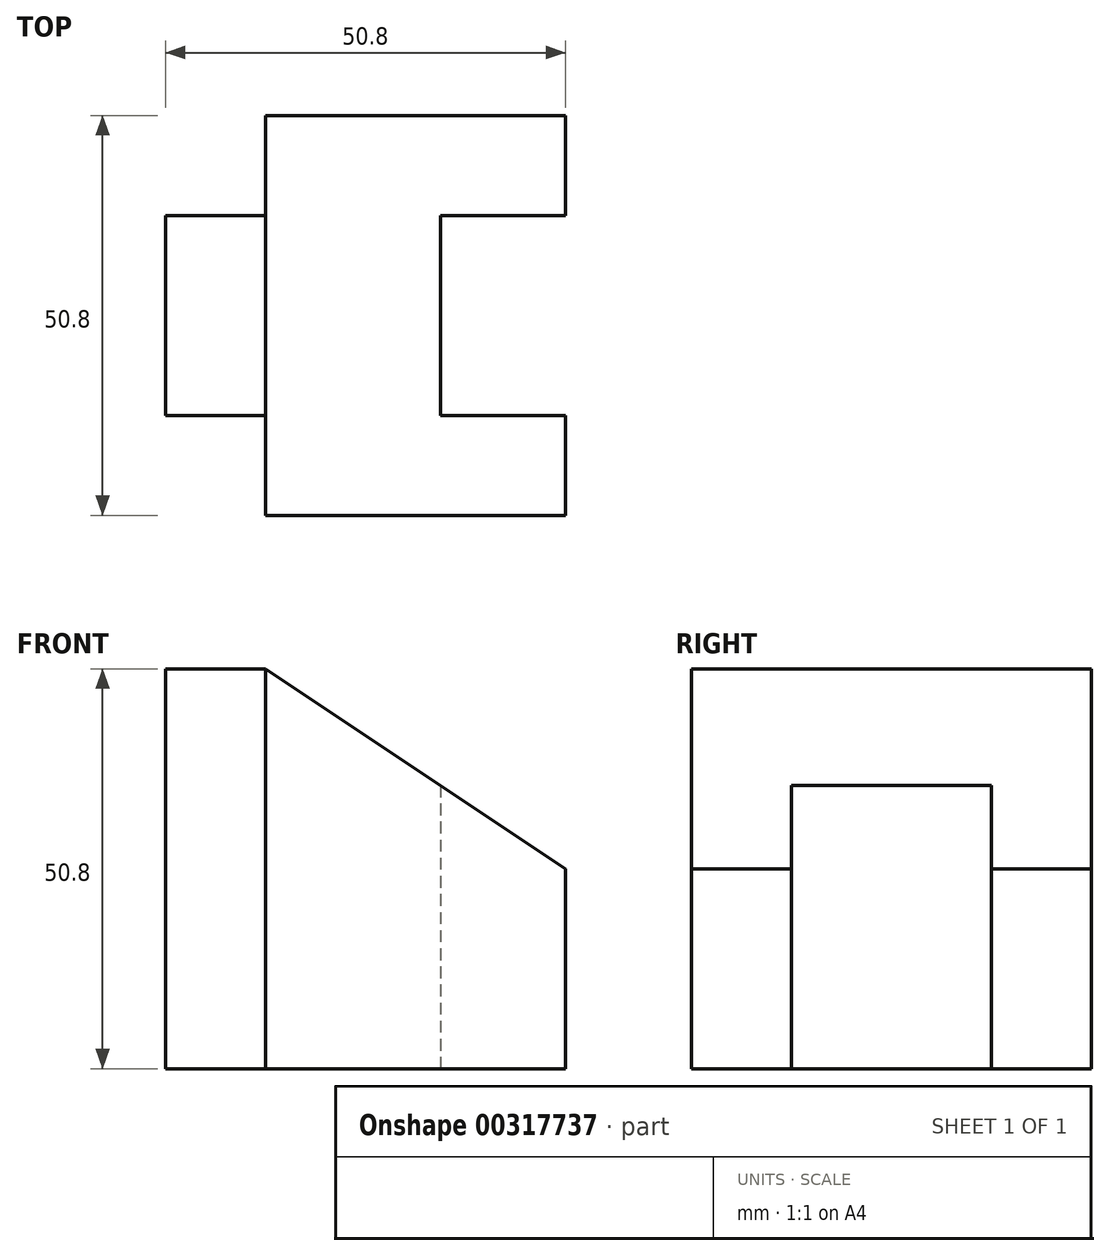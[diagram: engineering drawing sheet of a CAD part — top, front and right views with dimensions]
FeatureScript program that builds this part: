
annotation { "Feature Type Name" : "Feature", "Feature Type Description" : "" }
export const myFeature = defineFeature(function(context is Context, id is Id, definition is map)
    precondition{}
    {
        {
            var Q0;
            Q0=qCreatedBy(makeId("Front.planeOp"),FACE);
            var sketch = newSketch(context, id + "F0", { "sketchPlane" : qUnion([Q0])});
            skLineSegment(sketch, "E0", {"start": v(0, 0) * mm, "end": v(0, 50.8) * mm});
            skLineSegment(sketch, "E1", {"start": v(0, 50.8) * mm, "end": v(12.7, 50.8) * mm});
            skLineSegment(sketch, "E2", {"start": v(12.7, 50.8) * mm, "end": v(50.8, 25.4) * mm});
            skLineSegment(sketch, "E3", {"start": v(50.8, 25.4) * mm, "end": v(50.8, 0) * mm});
            skLineSegment(sketch, "E4", {"start": v(50.8, 0) * mm, "end": v(0, 0) * mm});
            skLineSegment(sketch, "E5", {"start": v(12.7, 50.8) * mm, "end": v(12.7, 0) * mm});
            skLineSegment(sketch, "E6", {"start": v(34.93, 35.98) * mm, "end": v(34.93, 0) * mm, "construction": true});
            skSolve(sketch);
        }
        {
            var Q0;
            Q0 = qSketchRegion(id + "F0", true);
            extrude(context, id + "F1", {"entities" : qUnion([Q0]), "depth" : 50.8 * mm});
        }
        {
            var Q0;
            Q0=makeQuery(id+"F1.opExtrude","SWEPT_FACE",FACE,{"disambiguationData":[OSD([sQuery(id+"F0.wireOp",EDGE,"E4")])]});
            var sketch = newSketch(context, id + "F2", { "sketchPlane" : qUnion([Q0])});
            skLineSegment(sketch, "E7", {"start": v(50.8, 50.8) * mm, "end": v(12.7, 50.8) * mm});
            skLineSegment(sketch, "E8", {"start": v(12.7, 50.8) * mm, "end": v(12.7, 38.1) * mm});
            skLineSegment(sketch, "E9", {"start": v(12.7, 38.1) * mm, "end": v(0, 38.1) * mm});
            skLineSegment(sketch, "E10", {"start": v(0, 38.1) * mm, "end": v(0, 12.7) * mm});
            skLineSegment(sketch, "E11", {"start": v(0, 12.7) * mm, "end": v(12.7, 12.7) * mm});
            skLineSegment(sketch, "E12", {"start": v(12.7, 12.7) * mm, "end": v(12.7, 0) * mm});
            skLineSegment(sketch, "E13", {"start": v(12.7, 0) * mm, "end": v(50.8, 0) * mm});
            skLineSegment(sketch, "E14", {"start": v(50.8, 0) * mm, "end": v(50.8, 12.7) * mm});
            skLineSegment(sketch, "E15", {"start": v(50.8, 12.7) * mm, "end": v(34.93, 12.7) * mm});
            skLineSegment(sketch, "E16", {"start": v(34.93, 12.7) * mm, "end": v(34.93, 38.1) * mm});
            skLineSegment(sketch, "E17", {"start": v(34.93, 38.1) * mm, "end": v(50.8, 38.1) * mm});
            skLineSegment(sketch, "E18", {"start": v(50.8, 38.1) * mm, "end": v(50.8, 50.8) * mm});
            skSolve(sketch);
        }
        {
            var Q0;
            {var subQ0=sQuery(id+"F2.wireOp",EDGE,"E8");Q0=makeQuery(id+"F2.imprint","IMPRINT",FACE,{"disambiguationData":[TD([[makeQuery(id+"F2.imprint","IMPRINT",EDGE,{"derivedFrom":subQ0}),-1.0]])]});}
            var Q1;
            {var subQ0=sQuery(id+"F2.wireOp",EDGE,"E11");Q1=makeQuery(id+"F2.imprint","IMPRINT",FACE,{"disambiguationData":[TD([[makeQuery(id+"F2.imprint","IMPRINT",EDGE,{"derivedFrom":subQ0}),-1.0]])]});}
            var Q2;
            {var subQ0=sQuery(id+"F2.wireOp",EDGE,"E15");Q2=makeQuery(id+"F2.imprint","IMPRINT",FACE,{"disambiguationData":[TD([[makeQuery(id+"F2.imprint","IMPRINT",EDGE,{"derivedFrom":subQ0}),-1.0]])]});}
            extrude(context, id + "F3", {"entities" : qUnion([Q0, Q1, Q2]), "operationType" : NewBodyOperationType.REMOVE, "endBound" : BoundingType.THROUGH_ALL, "oppositeDirection" : true, "depth" : 25.4 * mm});
        }
    });
